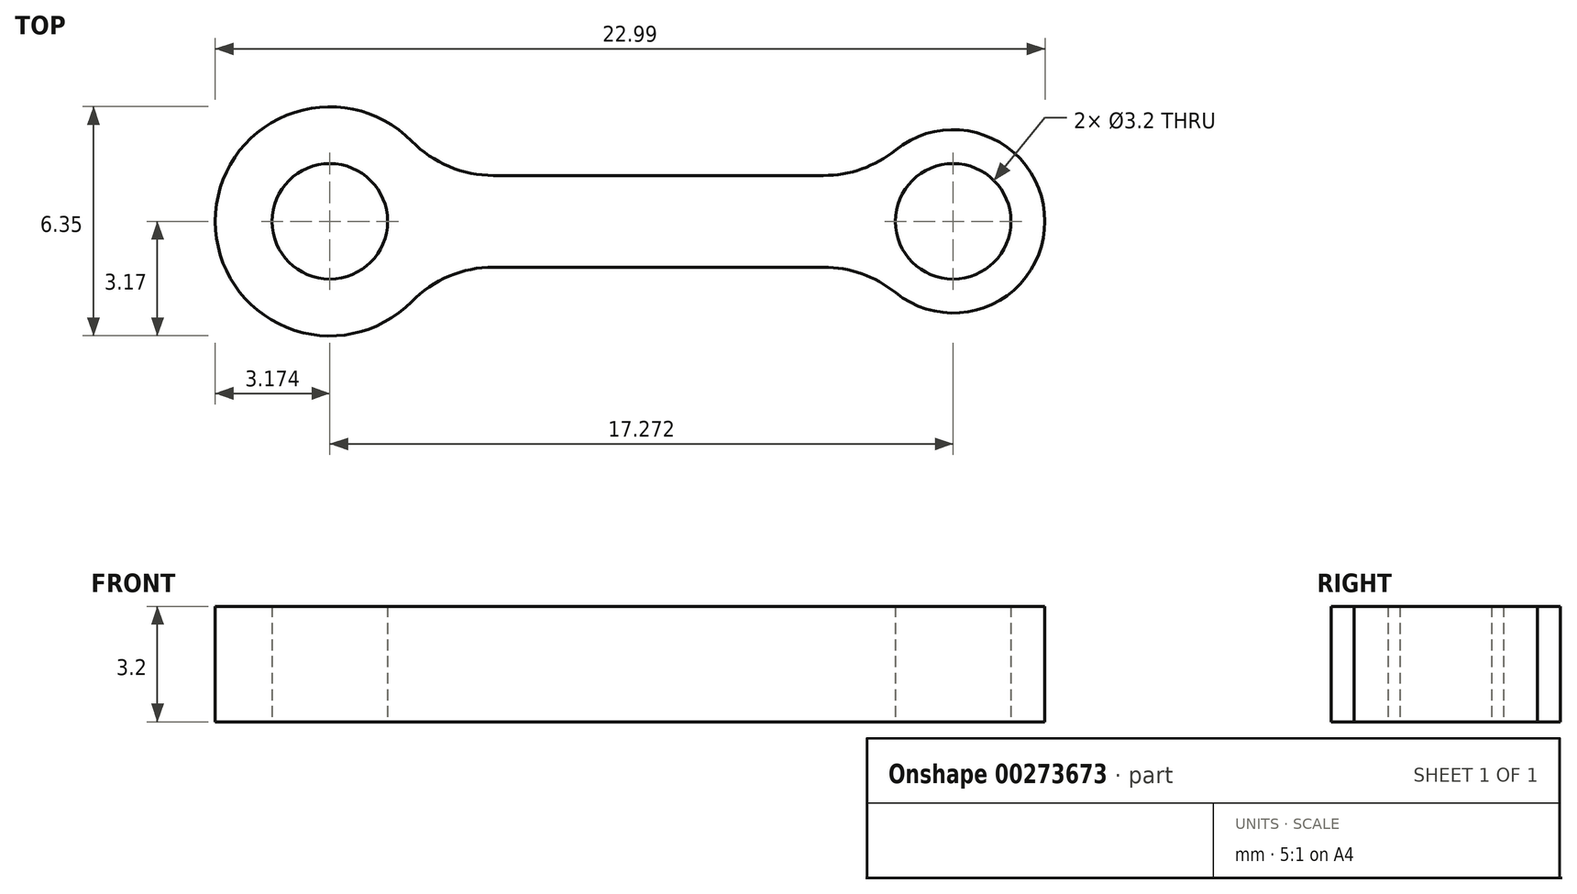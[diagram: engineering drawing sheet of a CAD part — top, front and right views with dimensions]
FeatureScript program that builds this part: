
annotation { "Feature Type Name" : "Feature", "Feature Type Description" : "" }
export const myFeature = defineFeature(function(context is Context, id is Id, definition is map)
    precondition{}
    {
        {
            var Q0;
            Q0=qCreatedBy(makeId("Top.planeOp"),FACE);
            var sketch = newSketch(context, id + "F0", { "sketchPlane" : qUnion([Q0])});
            skCircle(sketch, "E0", {"center": v(-8.64, 0) * mm, "radius": 1.6 * mm});
            skCircle(sketch, "E1", {"center": v(8.64, 0) * mm, "radius": 1.6 * mm});
            skArc(sketch, "E2", {"start": v(-6.37, 2.22) * mm, "mid": v(-11.81, 0) * mm, "end": v(-6.37, -2.22) * mm});
            skArc(sketch, "E3", {"start": v(7.04, -1.98) * mm, "mid": v(11.18, 0) * mm, "end": v(7.04, 1.98) * mm});
            skLineSegment(sketch, "E4", {"start": v(-4.1, 1.27) * mm, "end": v(5.04, 1.27) * mm});
            skLineSegment(sketch, "E5", {"start": v(-4.1, -1.27) * mm, "end": v(5.04, -1.27) * mm});
            skArc(sketch, "E6", {"start": v(-6.37, 2.22) * mm, "mid": v(-5.33, 1.52) * mm, "end": v(-4.1, 1.27) * mm});
            skArc(sketch, "E7.MirrorCS", {"start": v(-6.37, -2.22) * mm, "mid": v(-5.33, -1.52) * mm, "end": v(-4.1, -1.27) * mm});
            skArc(sketch, "E8", {"start": v(5.04, 1.27) * mm, "mid": v(6.1, 1.45) * mm, "end": v(7.04, 1.98) * mm});
            skPoint(sketch, "E9.orphan", {"position": v(5.04, 1.27) * mm});
            skArc(sketch, "E10.MirrorCS", {"start": v(5.04, -1.27) * mm, "mid": v(6.1, -1.45) * mm, "end": v(7.04, -1.98) * mm});
            skSolve(sketch);
        }
        {
            var Q0;
            Q0 = qSketchRegion(id + "F0", true);
            extrude(context, id + "F1", {"entities" : qUnion([Q0]), "depth" : 3.2 * mm});
        }
    });
